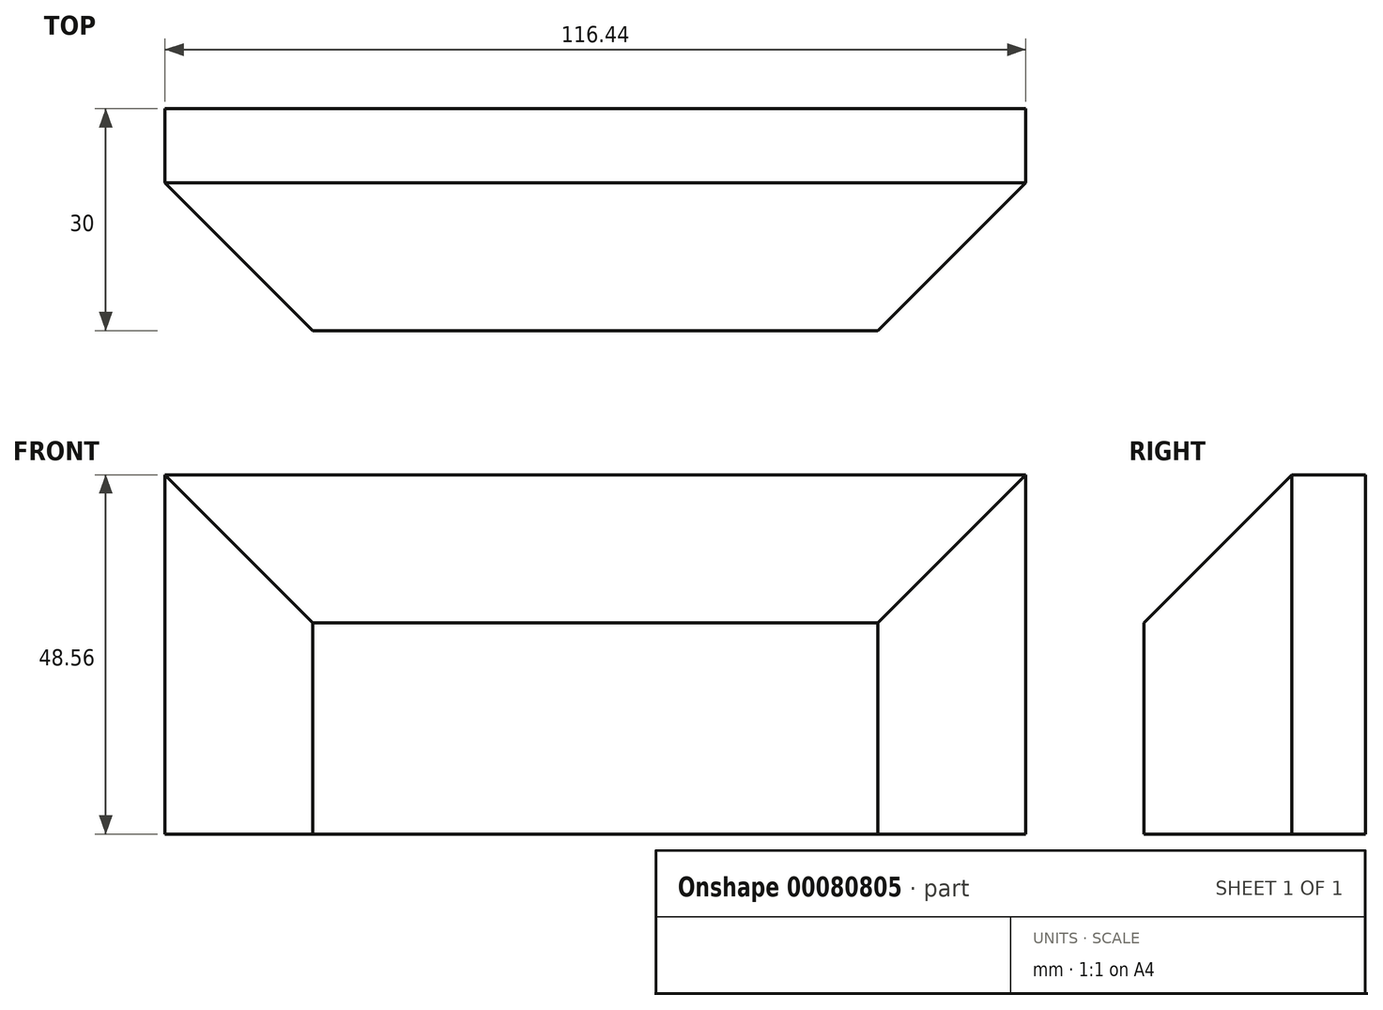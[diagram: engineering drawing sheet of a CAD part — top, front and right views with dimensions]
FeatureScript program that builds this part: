
annotation { "Feature Type Name" : "Feature", "Feature Type Description" : "" }
export const myFeature = defineFeature(function(context is Context, id is Id, definition is map)
    precondition{}
    {
        {
            var Q0;
            Q0=qCreatedBy(makeId("Front.planeOp"),FACE);
            var sketch = newSketch(context, id + "F0", { "sketchPlane" : qUnion([Q0])});
            skLineSegment(sketch, "E0.bottom", {"start": v(58.22, -24.28) * mm, "end": v(-58.22, -24.28) * mm});
            skLineSegment(sketch, "E0.top", {"start": v(58.22, 24.28) * mm, "end": v(-58.22, 24.28) * mm});
            skLineSegment(sketch, "E0.left", {"start": v(58.22, -24.28) * mm, "end": v(58.22, 24.28) * mm});
            skLineSegment(sketch, "E0.right", {"start": v(-58.22, -24.28) * mm, "end": v(-58.22, 24.28) * mm});
            skPoint(sketch, "E0.middle", {"position": v(0, 0) * mm});
            skSolve(sketch);
        }
        {
            var Q0;
            Q0=makeQuery(id+"F0.imprint","IMPRINT",FACE,{"disambiguationData":[TD([[makeQuery(id+"F0.imprint","IMPRINT",EDGE,{"derivedFrom":sQuery(id+"F0.wireOp",EDGE,"E0.bottom")}),-1.0]])]});
            extrude(context, id + "F1", {"entities" : qUnion([Q0]), "depth" : 30 * mm});
        }
        {
            var Q0;
            Q0=makeQuery(id+"F1.opExtrude","CAP_EDGE",EDGE,{"disambiguationData":[OSD([sQuery(id+"F0.wireOp",EDGE,"E0.top")])],"isStart":false});
            chamfer(context, id + "F2", {"entities" : qUnion([Q0]), "width" : 20 * mm, "tangentPropagation" : true});
        }
        {
            var Q0;
            Q0=makeQuery(id+"F1.opExtrude","CAP_EDGE",EDGE,{"disambiguationData":[OSD([sQuery(id+"F0.wireOp",EDGE,"E0.right")])],"isStart":false});
            var Q1;
            Q1=makeQuery(id+"F1.opExtrude","CAP_EDGE",EDGE,{"disambiguationData":[OSD([sQuery(id+"F0.wireOp",EDGE,"E0.left")])],"isStart":false});
            chamfer(context, id + "F3", {"entities" : qUnion([Q0, Q1]), "width" : 20 * mm, "tangentPropagation" : true});
        }
    });
